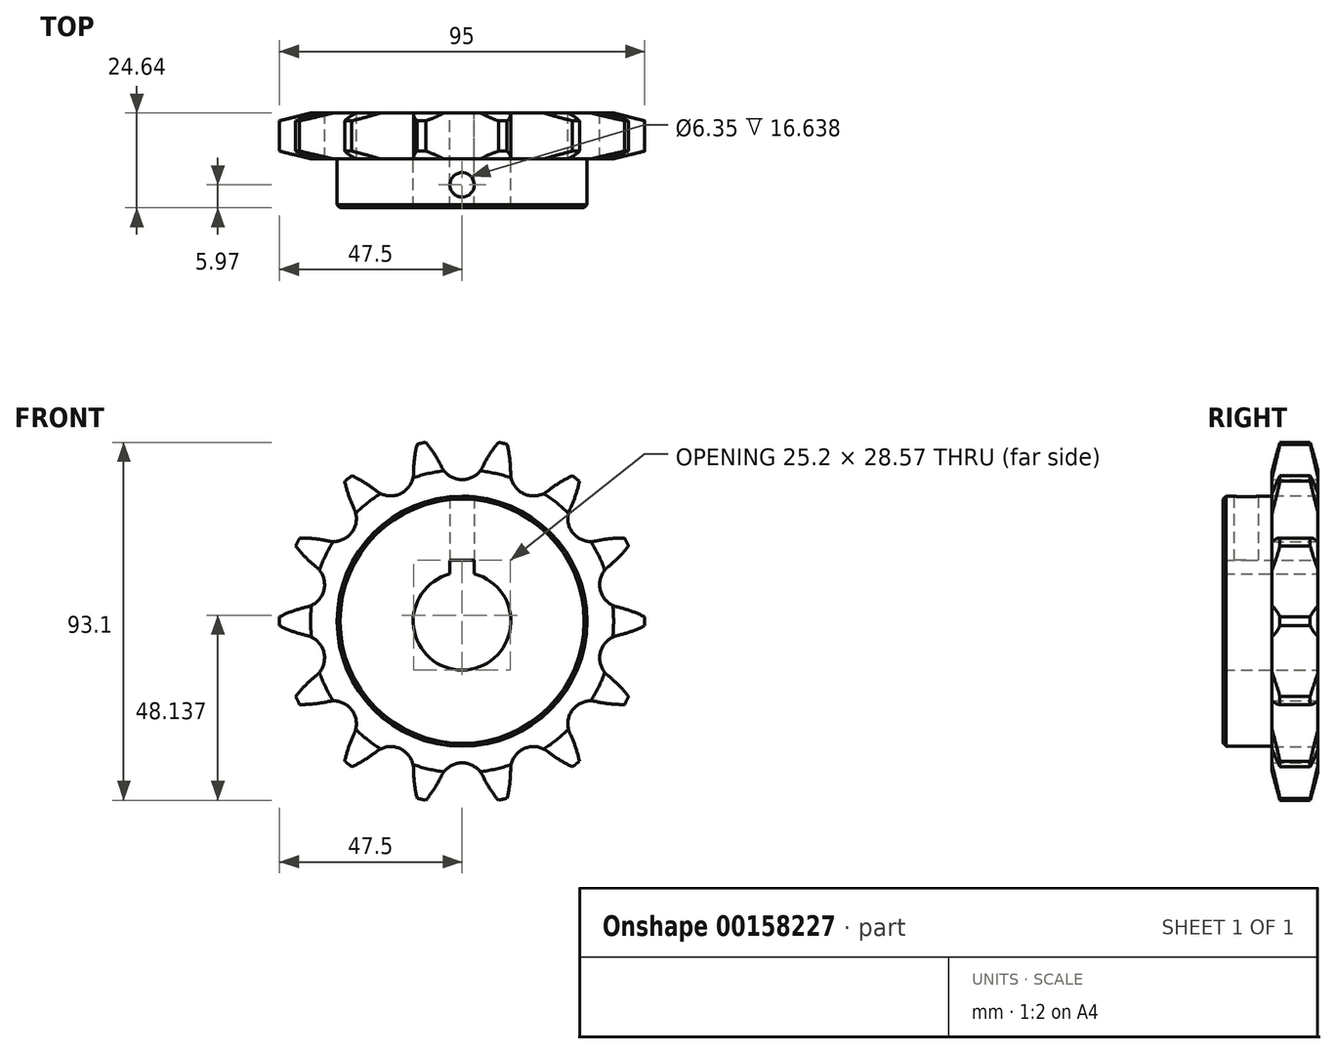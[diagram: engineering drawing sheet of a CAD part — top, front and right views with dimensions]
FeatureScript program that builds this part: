
annotation { "Feature Type Name" : "Feature", "Feature Type Description" : "" }
export const myFeature = defineFeature(function(context is Context, id is Id, definition is map)
    precondition{}
    {
        {
            var Q0;
            Q0=qCreatedBy(makeId("Front.planeOp"),FACE);
            var sketch = newSketch(context, id + "F0", { "sketchPlane" : qUnion([Q0])});
            skCircle(sketch, "E0", {"center": v(0, 0) * mm, "radius": 42.81 * mm, "construction": true});
            skLineSegment(sketch, "E1", {"start": v(0, 0) * mm, "end": v(0, 36.84) * mm});
            skLineSegment(sketch, "E2.1.0", {"start": v(0, 0) * mm, "end": v(-23.8, 49.42) * mm, "construction": true});
            skLineSegment(sketch, "E2.2.0", {"start": v(0, 0) * mm, "end": v(-42.89, 34.2) * mm, "construction": true});
            skLineSegment(sketch, "E2.3.0", {"start": v(0, 0) * mm, "end": v(-53.48, 12.2) * mm, "construction": true});
            skLineSegment(sketch, "E2.4.0", {"start": v(0, 0) * mm, "end": v(-53.48, -12.2) * mm, "construction": true});
            skLineSegment(sketch, "E2.5.0", {"start": v(0, 0) * mm, "end": v(-42.89, -34.2) * mm, "construction": true});
            skLineSegment(sketch, "E2.6.0", {"start": v(0, 0) * mm, "end": v(-23.8, -49.42) * mm, "construction": true});
            skLineSegment(sketch, "E2.7.0", {"start": v(0, 0) * mm, "end": v(0, -54.86) * mm, "construction": true});
            skLineSegment(sketch, "E2.8.0", {"start": v(0, 0) * mm, "end": v(23.8, -49.42) * mm, "construction": true});
            skLineSegment(sketch, "E2.9.0", {"start": v(0, 0) * mm, "end": v(42.89, -34.2) * mm, "construction": true});
            skLineSegment(sketch, "E2.10.0", {"start": v(0, 0) * mm, "end": v(53.48, -12.2) * mm, "construction": true});
            skLineSegment(sketch, "E2.11.0", {"start": v(0, 0) * mm, "end": v(53.48, 12.2) * mm, "construction": true});
            skLineSegment(sketch, "E2.12.0", {"start": v(0, 0) * mm, "end": v(38.14, 30.41) * mm, "construction": true});
            skLineSegment(sketch, "E2.13.0", {"start": v(0, 0) * mm, "end": v(15.99, 33.2) * mm});
            skArc(sketch, "E3", {"start": v(0, 36.84) * mm, "mid": v(3.18, 37.76) * mm, "end": v(5.38, 40.22) * mm});
            skArc(sketch, "E4", {"start": v(12.6, 38.57) * mm, "mid": v(13.52, 35.4) * mm, "end": v(15.99, 33.2) * mm});
            skArc(sketch, "E5", {"start": v(9.43, 46.55) * mm, "mid": v(7.21, 43.5) * mm, "end": v(5.38, 40.22) * mm});
            skArc(sketch, "E6.trimOffspring", {"start": v(11.7, 46.03) * mm, "mid": v(10.57, 46.3) * mm, "end": v(9.43, 46.55) * mm});
            skArc(sketch, "E7.trimOffspring", {"start": v(12.6, 38.57) * mm, "mid": v(12.38, 42.33) * mm, "end": v(11.7, 46.03) * mm});
            skPoint(sketch, "E8.orphan", {"position": v(42.89, 34.2) * mm});
            skPoint(sketch, "E9.orphan", {"position": v(23.8, 49.42) * mm});
            skPoint(sketch, "E10.orphan", {"position": v(0, 54.86) * mm});
            skLineSegment(sketch, "E11.1.0", {"start": v(0, 0) * mm, "end": v(-15.99, 33.2) * mm});
            skArc(sketch, "E11.1.1", {"start": v(-15.99, 33.2) * mm, "mid": v(-13.52, 35.4) * mm, "end": v(-12.6, 38.57) * mm});
            skArc(sketch, "E11.1.2", {"start": v(-11.7, 46.03) * mm, "mid": v(-12.38, 42.33) * mm, "end": v(-12.6, 38.57) * mm});
            skArc(sketch, "E11.1.3", {"start": v(-9.43, 46.55) * mm, "mid": v(-10.57, 46.3) * mm, "end": v(-11.7, 46.03) * mm});
            skArc(sketch, "E11.1.4", {"start": v(-5.38, 40.22) * mm, "mid": v(-7.21, 43.5) * mm, "end": v(-9.43, 46.55) * mm});
            skArc(sketch, "E11.1.5", {"start": v(-5.38, 40.22) * mm, "mid": v(-3.18, 37.76) * mm, "end": v(0, 36.84) * mm});
            skLineSegment(sketch, "E11.2.0", {"start": v(0, 0) * mm, "end": v(-28.8, 22.97) * mm});
            skArc(sketch, "E11.2.1", {"start": v(-28.8, 22.97) * mm, "mid": v(-27.54, 26.02) * mm, "end": v(-28.1, 29.28) * mm});
            skArc(sketch, "E11.2.2", {"start": v(-30.52, 36.4) * mm, "mid": v(-29.52, 32.77) * mm, "end": v(-28.1, 29.28) * mm});
            skArc(sketch, "E11.2.3", {"start": v(-28.7, 37.85) * mm, "mid": v(-29.61, 37.14) * mm, "end": v(-30.52, 36.4) * mm});
            skArc(sketch, "E11.2.4", {"start": v(-22.3, 33.9) * mm, "mid": v(-25.38, 36.07) * mm, "end": v(-28.7, 37.85) * mm});
            skArc(sketch, "E11.2.5", {"start": v(-22.3, 33.9) * mm, "mid": v(-19.24, 32.64) * mm, "end": v(-15.99, 33.2) * mm});
            skLineSegment(sketch, "E11.3.0", {"start": v(0, 0) * mm, "end": v(-35.92, 8.2) * mm});
            skArc(sketch, "E11.3.1", {"start": v(-35.92, 8.2) * mm, "mid": v(-36.1, 11.5) * mm, "end": v(-38.02, 14.2) * mm});
            skArc(sketch, "E11.3.2", {"start": v(-43.29, 19.55) * mm, "mid": v(-40.81, 16.71) * mm, "end": v(-38.02, 14.2) * mm});
            skArc(sketch, "E11.3.3", {"start": v(-42.28, 21.65) * mm, "mid": v(-42.8, 20.6) * mm, "end": v(-43.29, 19.55) * mm});
            skArc(sketch, "E11.3.4", {"start": v(-34.8, 20.87) * mm, "mid": v(-38.51, 21.49) * mm, "end": v(-42.28, 21.65) * mm});
            skArc(sketch, "E11.3.5", {"start": v(-34.8, 20.87) * mm, "mid": v(-31.5, 21.06) * mm, "end": v(-28.8, 22.97) * mm});
            skLineSegment(sketch, "E11.4.0", {"start": v(0, 0) * mm, "end": v(-35.92, -8.2) * mm});
            skArc(sketch, "E11.4.1", {"start": v(-35.92, -8.2) * mm, "mid": v(-37.52, -5.3) * mm, "end": v(-40.41, -3.7) * mm});
            skArc(sketch, "E11.4.2", {"start": v(-47.48, -1.16) * mm, "mid": v(-44.02, -2.65) * mm, "end": v(-40.41, -3.7) * mm});
            skArc(sketch, "E11.4.3", {"start": v(-47.48, 1.16) * mm, "mid": v(-47.5, 0) * mm, "end": v(-47.48, -1.16) * mm});
            skArc(sketch, "E11.4.4", {"start": v(-40.41, 3.7) * mm, "mid": v(-44.02, 2.65) * mm, "end": v(-47.48, 1.16) * mm});
            skArc(sketch, "E11.4.5", {"start": v(-40.41, 3.7) * mm, "mid": v(-37.52, 5.3) * mm, "end": v(-35.92, 8.2) * mm});
            skLineSegment(sketch, "E11.5.0", {"start": v(0, 0) * mm, "end": v(-28.8, -22.97) * mm});
            skArc(sketch, "E11.5.1", {"start": v(-28.8, -22.97) * mm, "mid": v(-31.5, -21.06) * mm, "end": v(-34.8, -20.87) * mm});
            skArc(sketch, "E11.5.2", {"start": v(-42.28, -21.65) * mm, "mid": v(-38.51, -21.49) * mm, "end": v(-34.8, -20.87) * mm});
            skArc(sketch, "E11.5.3", {"start": v(-43.29, -19.55) * mm, "mid": v(-42.8, -20.6) * mm, "end": v(-42.28, -21.65) * mm});
            skArc(sketch, "E11.5.4", {"start": v(-38.02, -14.2) * mm, "mid": v(-40.81, -16.71) * mm, "end": v(-43.29, -19.55) * mm});
            skArc(sketch, "E11.5.5", {"start": v(-38.02, -14.2) * mm, "mid": v(-36.1, -11.5) * mm, "end": v(-35.92, -8.2) * mm});
            skLineSegment(sketch, "E11.5.7", {"start": v(0, 0) * mm, "end": v(42.89, 34.2) * mm, "construction": true});
            skLineSegment(sketch, "E11.6.0", {"start": v(0, 0) * mm, "end": v(-15.99, -33.2) * mm});
            skArc(sketch, "E11.6.1", {"start": v(-15.99, -33.2) * mm, "mid": v(-19.24, -32.64) * mm, "end": v(-22.3, -33.9) * mm});
            skArc(sketch, "E11.6.2", {"start": v(-28.7, -37.85) * mm, "mid": v(-25.38, -36.07) * mm, "end": v(-22.3, -33.9) * mm});
            skArc(sketch, "E11.6.3", {"start": v(-30.52, -36.4) * mm, "mid": v(-29.61, -37.14) * mm, "end": v(-28.7, -37.85) * mm});
            skArc(sketch, "E11.6.4", {"start": v(-28.1, -29.28) * mm, "mid": v(-29.52, -32.77) * mm, "end": v(-30.52, -36.4) * mm});
            skArc(sketch, "E11.6.5", {"start": v(-28.1, -29.28) * mm, "mid": v(-27.54, -26.02) * mm, "end": v(-28.8, -22.97) * mm});
            skLineSegment(sketch, "E11.6.6", {"start": v(0, 0) * mm, "end": v(42.89, 34.2) * mm, "construction": true});
            skLineSegment(sketch, "E11.6.7", {"start": v(0, 0) * mm, "end": v(23.8, 49.42) * mm, "construction": true});
            skLineSegment(sketch, "E11.7.0", {"start": v(0, 0) * mm, "end": v(0, -36.84) * mm});
            skArc(sketch, "E11.7.1", {"start": v(0, -36.84) * mm, "mid": v(-3.18, -37.76) * mm, "end": v(-5.38, -40.22) * mm});
            skArc(sketch, "E11.7.2", {"start": v(-9.43, -46.55) * mm, "mid": v(-7.21, -43.5) * mm, "end": v(-5.38, -40.22) * mm});
            skArc(sketch, "E11.7.3", {"start": v(-11.7, -46.03) * mm, "mid": v(-10.57, -46.3) * mm, "end": v(-9.43, -46.55) * mm});
            skArc(sketch, "E11.7.4", {"start": v(-12.6, -38.57) * mm, "mid": v(-12.38, -42.33) * mm, "end": v(-11.7, -46.03) * mm});
            skArc(sketch, "E11.7.5", {"start": v(-12.6, -38.57) * mm, "mid": v(-13.52, -35.4) * mm, "end": v(-15.99, -33.2) * mm});
            skLineSegment(sketch, "E11.7.6", {"start": v(0, 0) * mm, "end": v(23.8, 49.42) * mm, "construction": true});
            skLineSegment(sketch, "E11.7.7", {"start": v(0, 0) * mm, "end": v(0, 54.86) * mm, "construction": true});
            skLineSegment(sketch, "E11.8.0", {"start": v(0, 0) * mm, "end": v(15.99, -33.2) * mm});
            skArc(sketch, "E11.8.1", {"start": v(15.99, -33.2) * mm, "mid": v(13.52, -35.4) * mm, "end": v(12.6, -38.57) * mm});
            skArc(sketch, "E11.8.2", {"start": v(11.7, -46.03) * mm, "mid": v(12.38, -42.33) * mm, "end": v(12.6, -38.57) * mm});
            skArc(sketch, "E11.8.3", {"start": v(9.43, -46.55) * mm, "mid": v(10.57, -46.3) * mm, "end": v(11.7, -46.03) * mm});
            skArc(sketch, "E11.8.4", {"start": v(5.38, -40.22) * mm, "mid": v(7.21, -43.5) * mm, "end": v(9.43, -46.55) * mm});
            skArc(sketch, "E11.8.5", {"start": v(5.38, -40.22) * mm, "mid": v(3.18, -37.76) * mm, "end": v(0, -36.84) * mm});
            skLineSegment(sketch, "E11.8.6", {"start": v(0, 0) * mm, "end": v(0, 54.86) * mm, "construction": true});
            skLineSegment(sketch, "E11.9.0", {"start": v(0, 0) * mm, "end": v(28.8, -22.97) * mm});
            skArc(sketch, "E11.9.1", {"start": v(28.8, -22.97) * mm, "mid": v(27.54, -26.02) * mm, "end": v(28.1, -29.28) * mm});
            skArc(sketch, "E11.9.2", {"start": v(30.52, -36.4) * mm, "mid": v(29.52, -32.77) * mm, "end": v(28.1, -29.28) * mm});
            skArc(sketch, "E11.9.3", {"start": v(28.7, -37.85) * mm, "mid": v(29.61, -37.14) * mm, "end": v(30.52, -36.4) * mm});
            skArc(sketch, "E11.9.4", {"start": v(22.3, -33.9) * mm, "mid": v(25.38, -36.07) * mm, "end": v(28.7, -37.85) * mm});
            skArc(sketch, "E11.9.5", {"start": v(22.3, -33.9) * mm, "mid": v(19.24, -32.64) * mm, "end": v(15.99, -33.2) * mm});
            skLineSegment(sketch, "E11.10.0", {"start": v(0, 0) * mm, "end": v(35.92, -8.2) * mm});
            skArc(sketch, "E11.10.1", {"start": v(35.92, -8.2) * mm, "mid": v(36.1, -11.5) * mm, "end": v(38.02, -14.2) * mm});
            skArc(sketch, "E11.10.2", {"start": v(43.29, -19.55) * mm, "mid": v(40.81, -16.71) * mm, "end": v(38.02, -14.2) * mm});
            skArc(sketch, "E11.10.3", {"start": v(42.28, -21.65) * mm, "mid": v(42.8, -20.6) * mm, "end": v(43.29, -19.55) * mm});
            skArc(sketch, "E11.10.4", {"start": v(34.8, -20.87) * mm, "mid": v(38.51, -21.49) * mm, "end": v(42.28, -21.65) * mm});
            skArc(sketch, "E11.10.5", {"start": v(34.8, -20.87) * mm, "mid": v(31.5, -21.06) * mm, "end": v(28.8, -22.97) * mm});
            skLineSegment(sketch, "E11.11.0", {"start": v(0, 0) * mm, "end": v(35.92, 8.2) * mm});
            skArc(sketch, "E11.11.1", {"start": v(35.92, 8.2) * mm, "mid": v(37.52, 5.3) * mm, "end": v(40.41, 3.7) * mm});
            skArc(sketch, "E11.11.2", {"start": v(47.48, 1.16) * mm, "mid": v(44.02, 2.65) * mm, "end": v(40.41, 3.7) * mm});
            skArc(sketch, "E11.11.3", {"start": v(47.48, -1.16) * mm, "mid": v(47.5, 0) * mm, "end": v(47.48, 1.16) * mm});
            skArc(sketch, "E11.11.4", {"start": v(40.41, -3.7) * mm, "mid": v(44.02, -2.65) * mm, "end": v(47.48, -1.16) * mm});
            skArc(sketch, "E11.11.5", {"start": v(40.41, -3.7) * mm, "mid": v(37.52, -5.3) * mm, "end": v(35.92, -8.2) * mm});
            skLineSegment(sketch, "E11.12.0", {"start": v(0, 0) * mm, "end": v(28.8, 22.97) * mm});
            skArc(sketch, "E11.12.1", {"start": v(28.8, 22.97) * mm, "mid": v(31.5, 21.06) * mm, "end": v(34.8, 20.87) * mm});
            skArc(sketch, "E11.12.2", {"start": v(42.28, 21.65) * mm, "mid": v(38.51, 21.49) * mm, "end": v(34.8, 20.87) * mm});
            skArc(sketch, "E11.12.3", {"start": v(43.29, 19.55) * mm, "mid": v(42.8, 20.6) * mm, "end": v(42.28, 21.65) * mm});
            skArc(sketch, "E11.12.4", {"start": v(38.02, 14.2) * mm, "mid": v(40.81, 16.71) * mm, "end": v(43.29, 19.55) * mm});
            skArc(sketch, "E11.12.5", {"start": v(38.02, 14.2) * mm, "mid": v(36.1, 11.5) * mm, "end": v(35.92, 8.2) * mm});
            skArc(sketch, "E11.13.1", {"start": v(15.99, 33.2) * mm, "mid": v(19.24, 32.64) * mm, "end": v(22.3, 33.9) * mm});
            skArc(sketch, "E11.13.2", {"start": v(28.7, 37.85) * mm, "mid": v(25.38, 36.07) * mm, "end": v(22.3, 33.9) * mm});
            skArc(sketch, "E11.13.3", {"start": v(30.52, 36.4) * mm, "mid": v(29.61, 37.14) * mm, "end": v(28.7, 37.85) * mm});
            skArc(sketch, "E11.13.4", {"start": v(28.1, 29.28) * mm, "mid": v(29.52, 32.77) * mm, "end": v(30.52, 36.4) * mm});
            skArc(sketch, "E11.13.5", {"start": v(28.1, 29.28) * mm, "mid": v(27.54, 26.02) * mm, "end": v(28.8, 22.97) * mm});
            skSolve(sketch);
        }
        {
            var Q0;
            Q0 = qSketchRegion(id + "F0", true);
            extrude(context, id + "F1", {"entities" : qUnion([Q0]), "endBound" : BoundingType.SYMMETRIC, "depth" : 11.94 * mm});
        }
        {
            var Q0;
            Q0=qCreatedBy(makeId("Right.planeOp"),FACE);
            var sketch = newSketch(context, id + "F2", { "sketchPlane" : qUnion([Q0])});
            skLineSegment(sketch, "E12", {"start": v(-3.26, 50.2) * mm, "end": v(-8.1, 30.94) * mm});
            skLineSegment(sketch, "E13", {"start": v(-8.1, 30.94) * mm, "end": v(-8.1, 50.2) * mm});
            skLineSegment(sketch, "E14", {"start": v(-8.1, 50.2) * mm, "end": v(-3.26, 50.2) * mm});
            skPoint(sketch, "E15.MirrorCS.end.orphan", {"position": v(-8.1, 50.2) * mm});
            skPoint(sketch, "E15.MirrorCS.start.orphan", {"position": v(-8.1, 69.47) * mm});
            skPoint(sketch, "E16.MirrorCS.start.orphan", {"position": v(-3.26, 50.2) * mm});
            skLineSegment(sketch, "E17.MirrorCS", {"start": v(8.1, 50.2) * mm, "end": v(3.26, 50.2) * mm});
            skLineSegment(sketch, "E18.MirrorCS", {"start": v(8.1, 30.94) * mm, "end": v(8.1, 50.2) * mm});
            skLineSegment(sketch, "E19.MirrorCS", {"start": v(3.26, 50.2) * mm, "end": v(8.1, 30.94) * mm});
            skSolve(sketch);
        }
        {
            var Q0;
            Q0=qCreatedBy(makeId("Top.planeOp"),FACE);
            var sketch = newSketch(context, id + "F3", { "sketchPlane" : qUnion([Q0])});
            skLineSegment(sketch, "E20", {"start": v(0, 0) * mm, "end": v(0, -59.47) * mm, "construction": true});
            skSolve(sketch);
        }
        {
            var Q0;
            Q0=makeQuery(id+"F2.imprint","IMPRINT",FACE,{"disambiguationData":[TD([[makeQuery(id+"F2.imprint","IMPRINT",EDGE,{"derivedFrom":sQuery(id+"F2.wireOp",EDGE,"E17.MirrorCS")}),1.0]])]});
            var Q1;
            Q1=makeQuery(id+"F2.imprint","IMPRINT",FACE,{"disambiguationData":[TD([[makeQuery(id+"F2.imprint","IMPRINT",EDGE,{"derivedFrom":sQuery(id+"F2.wireOp",EDGE,"E12")}),-1.0]])]});
            var Q2;
            Q2=sQuery(id+"F3.wireOp",EDGE,"E20");
            revolve(context, id + "F4", {"operationType" : NewBodyOperationType.REMOVE, "entities" : qUnion([Q0, Q1]), "axis" : qUnion([Q2]), "revolveType" : RevolveType.FULL, "oppositeDirection" : true});
        }
        {
            var Q0;
            Q0=makeQuery(id+"F1.opExtrude","CAP_FACE",FACE,{"disambiguationData":[OSD([sQuery(id+"F0.wireOp",EDGE,"E3"),sQuery(id+"F0.wireOp",EDGE,"E4"),sQuery(id+"F0.wireOp",EDGE,"E5"),sQuery(id+"F0.wireOp",EDGE,"E6.trimOffspring"),sQuery(id+"F0.wireOp",EDGE,"E7.trimOffspring"),sQuery(id+"F0.wireOp",EDGE,"E11.1.1"),sQuery(id+"F0.wireOp",EDGE,"E11.1.2"),sQuery(id+"F0.wireOp",EDGE,"E11.1.3"),sQuery(id+"F0.wireOp",EDGE,"E11.1.4"),sQuery(id+"F0.wireOp",EDGE,"E11.1.5"),sQuery(id+"F0.wireOp",EDGE,"E11.2.1"),sQuery(id+"F0.wireOp",EDGE,"E11.2.2"),sQuery(id+"F0.wireOp",EDGE,"E11.2.3"),sQuery(id+"F0.wireOp",EDGE,"E11.2.4"),sQuery(id+"F0.wireOp",EDGE,"E11.2.5"),sQuery(id+"F0.wireOp",EDGE,"E11.3.1"),sQuery(id+"F0.wireOp",EDGE,"E11.3.2"),sQuery(id+"F0.wireOp",EDGE,"E11.3.3"),sQuery(id+"F0.wireOp",EDGE,"E11.3.4"),sQuery(id+"F0.wireOp",EDGE,"E11.3.5"),sQuery(id+"F0.wireOp",EDGE,"E11.4.1"),sQuery(id+"F0.wireOp",EDGE,"E11.4.2"),sQuery(id+"F0.wireOp",EDGE,"E11.4.3"),sQuery(id+"F0.wireOp",EDGE,"E11.4.4"),sQuery(id+"F0.wireOp",EDGE,"E11.4.5"),sQuery(id+"F0.wireOp",EDGE,"E11.5.1"),sQuery(id+"F0.wireOp",EDGE,"E11.5.2"),sQuery(id+"F0.wireOp",EDGE,"E11.5.3"),sQuery(id+"F0.wireOp",EDGE,"E11.5.4"),sQuery(id+"F0.wireOp",EDGE,"E11.5.5"),sQuery(id+"F0.wireOp",EDGE,"E11.6.1"),sQuery(id+"F0.wireOp",EDGE,"E11.6.2"),sQuery(id+"F0.wireOp",EDGE,"E11.6.3"),sQuery(id+"F0.wireOp",EDGE,"E11.6.4"),sQuery(id+"F0.wireOp",EDGE,"E11.6.5"),sQuery(id+"F0.wireOp",EDGE,"E11.7.1"),sQuery(id+"F0.wireOp",EDGE,"E11.7.2"),sQuery(id+"F0.wireOp",EDGE,"E11.7.3"),sQuery(id+"F0.wireOp",EDGE,"E11.7.4"),sQuery(id+"F0.wireOp",EDGE,"E11.7.5"),sQuery(id+"F0.wireOp",EDGE,"E11.8.1"),sQuery(id+"F0.wireOp",EDGE,"E11.8.2"),sQuery(id+"F0.wireOp",EDGE,"E11.8.3"),sQuery(id+"F0.wireOp",EDGE,"E11.8.4"),sQuery(id+"F0.wireOp",EDGE,"E11.8.5"),sQuery(id+"F0.wireOp",EDGE,"E11.9.1"),sQuery(id+"F0.wireOp",EDGE,"E11.9.2"),sQuery(id+"F0.wireOp",EDGE,"E11.9.3"),sQuery(id+"F0.wireOp",EDGE,"E11.9.4"),sQuery(id+"F0.wireOp",EDGE,"E11.9.5"),sQuery(id+"F0.wireOp",EDGE,"E11.10.1"),sQuery(id+"F0.wireOp",EDGE,"E11.10.2"),sQuery(id+"F0.wireOp",EDGE,"E11.10.3"),sQuery(id+"F0.wireOp",EDGE,"E11.10.4"),sQuery(id+"F0.wireOp",EDGE,"E11.10.5"),sQuery(id+"F0.wireOp",EDGE,"E11.11.1"),sQuery(id+"F0.wireOp",EDGE,"E11.11.2"),sQuery(id+"F0.wireOp",EDGE,"E11.11.3"),sQuery(id+"F0.wireOp",EDGE,"E11.11.4"),sQuery(id+"F0.wireOp",EDGE,"E11.11.5"),sQuery(id+"F0.wireOp",EDGE,"E11.12.1"),sQuery(id+"F0.wireOp",EDGE,"E11.12.2"),sQuery(id+"F0.wireOp",EDGE,"E11.12.3"),sQuery(id+"F0.wireOp",EDGE,"E11.12.4"),sQuery(id+"F0.wireOp",EDGE,"E11.12.5"),sQuery(id+"F0.wireOp",EDGE,"E11.13.1"),sQuery(id+"F0.wireOp",EDGE,"E11.13.2"),sQuery(id+"F0.wireOp",EDGE,"E11.13.3"),sQuery(id+"F0.wireOp",EDGE,"E11.13.4"),sQuery(id+"F0.wireOp",EDGE,"E11.13.5")])],"isStart":false});
            var sketch = newSketch(context, id + "F5", { "sketchPlane" : qUnion([Q0])});
            skCircle(sketch, "E21", {"center": v(0, 0) * mm, "radius": 32.51 * mm});
            skSolve(sketch);
        }
        {
            var Q0;
            Q0 = qSketchRegion(id + "F5", true);
            extrude(context, id + "F6", {"entities" : qUnion([Q0]), "operationType" : NewBodyOperationType.ADD, "depth" : 12.7 * mm});
        }
        {
            var Q0;
            Q0=qCreatedBy(makeId("Front.planeOp"),FACE);
            var sketch = newSketch(context, id + "F7", { "sketchPlane" : qUnion([Q0])});
            skArc(sketch, "E22", {"start": v(-3.17, 12.3) * mm, "mid": v(0, -12.7) * mm, "end": v(3.18, 12.3) * mm});
            skLineSegment(sketch, "E23.bottom", {"start": v(3.18, 15.88) * mm, "end": v(-3.17, 15.88) * mm});
            skLineSegment(sketch, "E23.left", {"start": v(3.18, 15.88) * mm, "end": v(3.18, 12.3) * mm});
            skLineSegment(sketch, "E23.right", {"start": v(-3.17, 15.88) * mm, "end": v(-3.17, 12.3) * mm});
            skPoint(sketch, "E23.middle", {"position": v(0, 12.7) * mm});
            skPoint(sketch, "E23.top.end.orphan", {"position": v(-3.17, 9.53) * mm});
            skPoint(sketch, "E24.orphan", {"position": v(3.18, 9.53) * mm});
            skSolve(sketch);
        }
        {
            var Q0;
            Q0 = qSketchRegion(id + "F7", true);
            extrude(context, id + "F8", {"entities" : qUnion([Q0]), "operationType" : NewBodyOperationType.REMOVE, "endBound" : BoundingType.SYMMETRIC, "depth" : 101.6 * mm});
        }
        {
            var Q0;
            Q0=makeQuery(id+"F6.opExtrude","CAP_EDGE",EDGE,{"disambiguationData":[OSD([sQuery(id+"F5.wireOp",EDGE,"E21")])],"isStart":false});
            chamfer(context, id + "F9", {"entities" : qUnion([Q0]), "width" : 0.76 * mm, "tangentPropagation" : true});
        }
        {
            var Q0;
            Q0=qCreatedBy(makeId("Top.planeOp"),FACE);
            var sketch = newSketch(context, id + "F10", { "sketchPlane" : qUnion([Q0])});
            skCircle(sketch, "E25", {"center": v(0, -12.7) * mm, "radius": 3.18 * mm});
            skSolve(sketch);
        }
        {
            var Q0;
            Q0=makeQuery(id+"F10.imprint","IMPRINT",FACE,{"disambiguationData":[TD([[makeQuery(id+"F10.imprint","IMPRINT",EDGE,{"derivedFrom":sQuery(id+"F10.wireOp",EDGE,"E25")}),1.0]])]});
            extrude(context, id + "F11", {"entities" : qUnion([Q0]), "operationType" : NewBodyOperationType.REMOVE, "depth" : 76.2 * mm});
        }
    });
